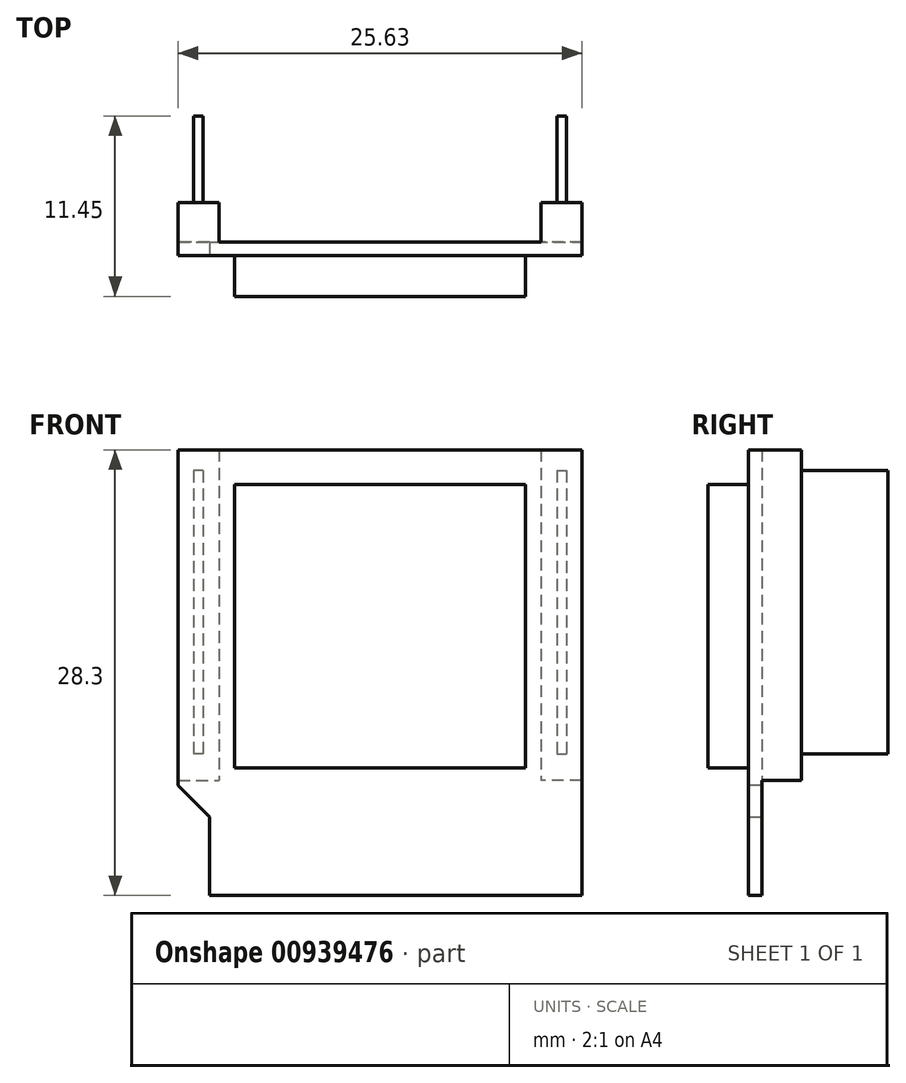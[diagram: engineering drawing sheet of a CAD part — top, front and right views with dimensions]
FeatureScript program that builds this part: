
annotation { "Feature Type Name" : "Feature", "Feature Type Description" : "" }
export const myFeature = defineFeature(function(context is Context, id is Id, definition is map)
    precondition{}
    {
        {
            var Q0;
            Q0=qCreatedBy(makeId("Front.planeOp"),FACE);
            var sketch = newSketch(context, id + "F0", { "sketchPlane" : qUnion([Q0])});
            skLineSegment(sketch, "E0.bottom", {"start": v(0, 0) * mm, "end": v(25.63, 0) * mm});
            skLineSegment(sketch, "E0.top", {"start": v(0, -28.3) * mm, "end": v(25.63, -28.3) * mm});
            skLineSegment(sketch, "E0.left", {"start": v(0, 0) * mm, "end": v(0, -28.3) * mm});
            skLineSegment(sketch, "E0.right", {"start": v(25.63, 0) * mm, "end": v(25.63, -28.3) * mm});
            skSolve(sketch);
        }
        {
            var Q0;
            Q0 = qSketchRegion(id + "F0", true);
            extrude(context, id + "F1", {"entities" : qUnion([Q0]), "depth" : .85 * mm, "offsetDistance" : 25 * mm});
        }
        {
            var Q0;
            Q0=makeQuery(id+"F1.opExtrude","CAP_FACE",FACE,{"disambiguationData":[OSD([sQuery(id+"F0.wireOp",EDGE,"E0.bottom"),sQuery(id+"F0.wireOp",EDGE,"E0.top"),sQuery(id+"F0.wireOp",EDGE,"E0.left"),sQuery(id+"F0.wireOp",EDGE,"E0.right")])],"isStart":false});
            var sketch = newSketch(context, id + "F2", { "sketchPlane" : qUnion([Q0])});
            skLineSegment(sketch, "E1", {"start": v(12.81, 0) * mm, "end": v(12.81, -28.3) * mm, "construction": true});
            skLineSegment(sketch, "E2.bottom", {"start": v(12.81, -2.2) * mm, "end": v(3.56, -2.2) * mm});
            skLineSegment(sketch, "E2.top", {"start": v(12.82, -20.2) * mm, "end": v(3.57, -20.2) * mm});
            skLineSegment(sketch, "E2.left", {"start": v(12.81, -2.2) * mm, "end": v(12.81, -20.2) * mm});
            skLineSegment(sketch, "E2.right", {"start": v(3.56, -2.2) * mm, "end": v(3.57, -20.2) * mm});
            skLineSegment(sketch, "E3.MirrorCS", {"start": v(12.82, -2.2) * mm, "end": v(22.07, -2.2) * mm});
            skLineSegment(sketch, "E4.MirrorCS", {"start": v(22.07, -2.2) * mm, "end": v(22.06, -20.2) * mm});
            skLineSegment(sketch, "E5.MirrorCS", {"start": v(12.81, -20.2) * mm, "end": v(22.06, -20.2) * mm});
            skSolve(sketch);
        }
        {
            var Q0;
            Q0 = qSketchRegion(id + "F2", true);
            extrude(context, id + "F3", {"entities" : qUnion([Q0]), "operationType" : NewBodyOperationType.ADD, "depth" : 2.6 * mm, "offsetDistance" : 25 * mm});
        }
        {
            var Q0;
            Q0=makeQuery(id+"F1.opExtrude","CAP_FACE",FACE,{"disambiguationData":[OSD([sQuery(id+"F0.wireOp",EDGE,"E0.bottom"),sQuery(id+"F0.wireOp",EDGE,"E0.top"),sQuery(id+"F0.wireOp",EDGE,"E0.left"),sQuery(id+"F0.wireOp",EDGE,"E0.right")])],"isStart":false});
            var sketch = newSketch(context, id + "F4", { "sketchPlane" : qUnion([Q0])});
            skLineSegment(sketch, "E6.bottom", {"start": v(0, -28.3) * mm, "end": v(2, -28.3) * mm});
            skLineSegment(sketch, "E6.top", {"start": v(0, -21.3) * mm, "end": v(2, -21.3) * mm});
            skLineSegment(sketch, "E6.left", {"start": v(0, -28.3) * mm, "end": v(0, -21.3) * mm});
            skLineSegment(sketch, "E6.right", {"start": v(2, -28.3) * mm, "end": v(2, -21.3) * mm});
            skSolve(sketch);
        }
        {
            var Q0;
            Q0 = qSketchRegion(id + "F4", true);
            extrude(context, id + "F5", {"entities" : qUnion([Q0]), "operationType" : NewBodyOperationType.REMOVE, "oppositeDirection" : true, "depth" : 25 * mm, "offsetDistance" : 25 * mm});
        }
        {
            var Q0;
            Q0=makeQuery(id+"F5.boolean.opBoolean","COPY",EDGE,{"derivedFrom":makeQuery(id+"F5.opExtrude","SWEPT_EDGE",EDGE,{"disambiguationData":[OSD([sQuery(id+"F4.wireOp",EDGE,"E6.top"),sQuery(id+"F4.wireOp",EDGE,"E6.right")])]})});
            chamfer(context, id + "F6", {"entities" : qUnion([Q0]), "width" : 2 * mm, "tangentPropagation" : true});
        }
        {
            var Q0;
            Q0=makeQuery(id+"F1.opExtrude","CAP_FACE",FACE,{"disambiguationData":[OSD([sQuery(id+"F0.wireOp",EDGE,"E0.bottom"),sQuery(id+"F0.wireOp",EDGE,"E0.top"),sQuery(id+"F0.wireOp",EDGE,"E0.left"),sQuery(id+"F0.wireOp",EDGE,"E0.right")])],"isStart":true});
            var sketch = newSketch(context, id + "F7", { "sketchPlane" : qUnion([Q0])});
            skLineSegment(sketch, "E7", {"start": v(-12.81, 0) * mm, "end": v(-12.81, -28.3) * mm, "construction": true});
            skLineSegment(sketch, "E8.bottom", {"start": v(0, 0) * mm, "end": v(-2.6, 0) * mm});
            skLineSegment(sketch, "E8.top", {"start": v(0, -21) * mm, "end": v(-2.6, -21) * mm});
            skLineSegment(sketch, "E8.left", {"start": v(0, 0) * mm, "end": v(0, -21) * mm});
            skLineSegment(sketch, "E8.right", {"start": v(-2.6, 0) * mm, "end": v(-2.6, -21) * mm});
            skLineSegment(sketch, "E9.MirrorCS", {"start": v(-25.63, 0) * mm, "end": v(-23.03, 0) * mm});
            skLineSegment(sketch, "E10.MirrorCS", {"start": v(-25.63, -21) * mm, "end": v(-23.03, -21) * mm});
            skLineSegment(sketch, "E11.MirrorCS", {"start": v(-23.03, 0) * mm, "end": v(-23.03, -21) * mm});
            skLineSegment(sketch, "E12.MirrorCS", {"start": v(-25.63, 0) * mm, "end": v(-25.63, -21) * mm});
            skSolve(sketch);
        }
        {
            var Q0;
            Q0 = qSketchRegion(id + "F7", true);
            extrude(context, id + "F8", {"entities" : qUnion([Q0]), "operationType" : NewBodyOperationType.ADD, "depth" : 2.5 * mm, "offsetDistance" : 25 * mm});
        }
        {
            var Q0;
            Q0=makeQuery(id+"F8.opExtrude","CAP_FACE",FACE,{"disambiguationData":[OSD([sQuery(id+"F7.wireOp",EDGE,"E9.MirrorCS"),sQuery(id+"F7.wireOp",EDGE,"E10.MirrorCS"),sQuery(id+"F7.wireOp",EDGE,"E11.MirrorCS"),sQuery(id+"F7.wireOp",EDGE,"E12.MirrorCS")])],"isStart":false});
            var sketch = newSketch(context, id + "F9", { "sketchPlane" : qUnion([Q0])});
            skPoint(sketch, "E13.0", {"position": v(-12.81, 0) * mm});
            skLineSegment(sketch, "E14", {"start": v(-12.81, 0) * mm, "end": v(-12.81, -28.53) * mm, "construction": true});
            skLineSegment(sketch, "E15.bottom", {"start": v(-1.57, -1.31) * mm, "end": v(-0.97, -1.31) * mm});
            skLineSegment(sketch, "E15.top", {"start": v(-1.57, -19.31) * mm, "end": v(-0.97, -19.31) * mm});
            skLineSegment(sketch, "E15.left", {"start": v(-1.57, -1.31) * mm, "end": v(-1.57, -19.31) * mm});
            skLineSegment(sketch, "E15.right", {"start": v(-0.97, -1.31) * mm, "end": v(-0.97, -19.31) * mm});
            skLineSegment(sketch, "E16.MirrorCS", {"start": v(-24.06, -1.31) * mm, "end": v(-24.66, -1.31) * mm});
            skLineSegment(sketch, "E17.MirrorCS", {"start": v(-24.06, -19.31) * mm, "end": v(-24.66, -19.31) * mm});
            skLineSegment(sketch, "E18.MirrorCS", {"start": v(-24.06, -1.31) * mm, "end": v(-24.06, -19.31) * mm});
            skLineSegment(sketch, "E19.MirrorCS", {"start": v(-24.66, -1.31) * mm, "end": v(-24.66, -19.31) * mm});
            skSolve(sketch);
        }
        {
            var Q0;
            Q0 = qSketchRegion(id + "F9", true);
            extrude(context, id + "F10", {"entities" : qUnion([Q0]), "operationType" : NewBodyOperationType.ADD, "depth" : 5.5 * mm, "offsetDistance" : 25 * mm});
        }
    });
